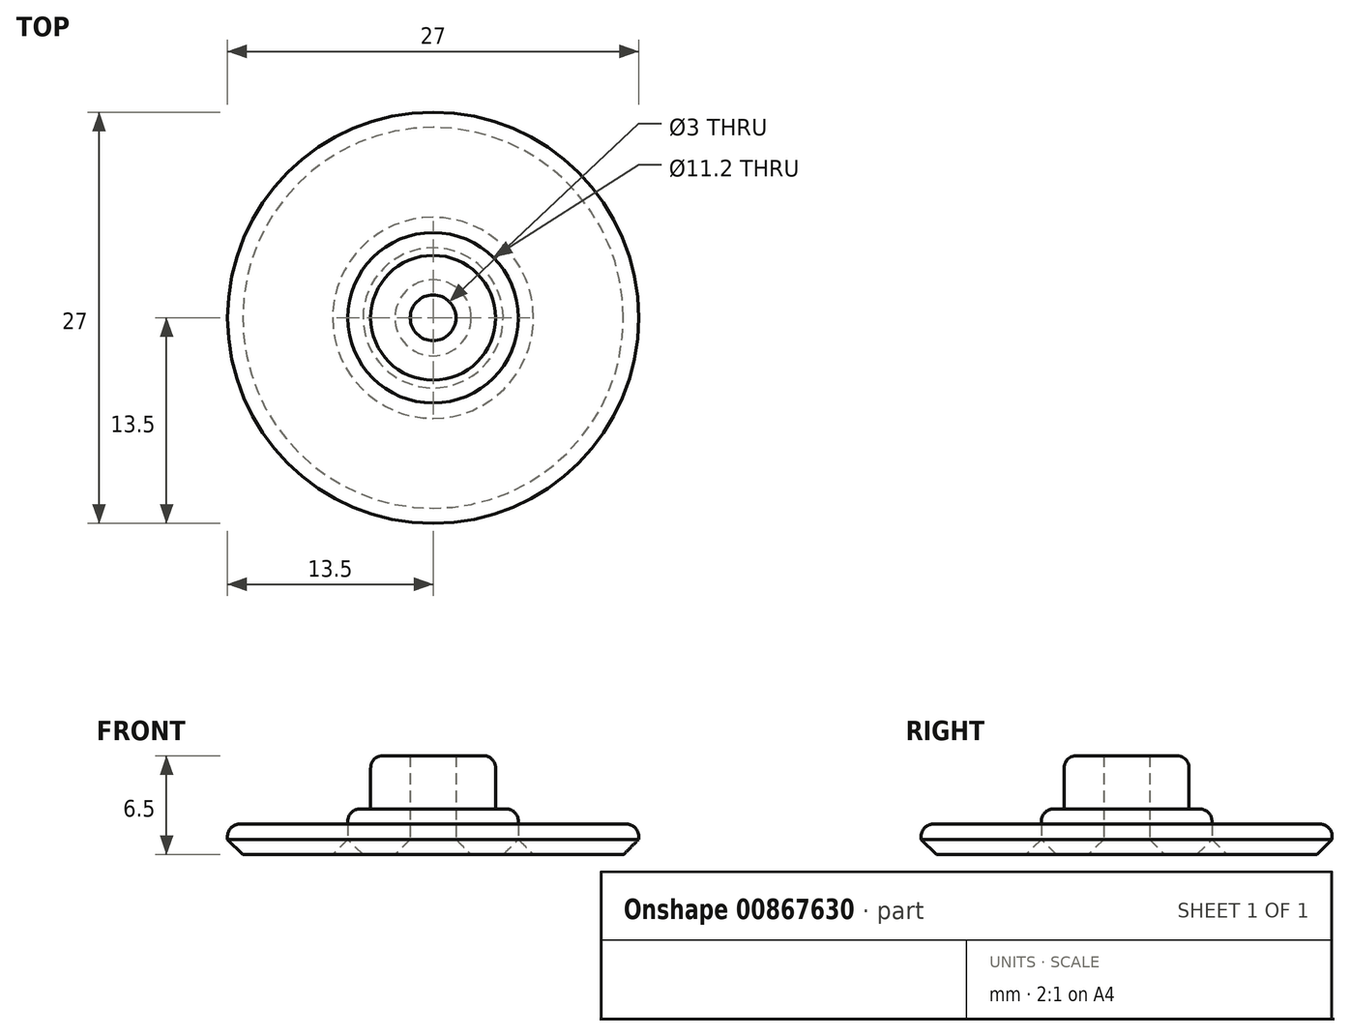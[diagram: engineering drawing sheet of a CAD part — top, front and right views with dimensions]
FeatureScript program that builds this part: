
annotation { "Feature Type Name" : "Feature", "Feature Type Description" : "" }
export const myFeature = defineFeature(function(context is Context, id is Id, definition is map)
    precondition{}
    {
        {
            var Q0;
            Q0=qCreatedBy(makeId("Top.planeOp"),FACE);
            var sketch = newSketch(context, id + "F0", { "sketchPlane" : qUnion([Q0])});
            skCircle(sketch, "E0", {"center": v(0, 0) * mm, "radius": 13.5 * mm});
            skCircle(sketch, "E1", {"center": v(0, 0) * mm, "radius": 5.6 * mm});
            skCircle(sketch, "E2", {"center": v(0, 0) * mm, "radius": 4.1 * mm});
            skCircle(sketch, "E3", {"center": v(0, 0) * mm, "radius": 1.5 * mm});
            skSolve(sketch);
        }
        {
            var Q0;
            Q0=makeQuery(id+"F0.imprint","IMPRINT",FACE,{"disambiguationData":[TD([[makeQuery(id+"F0.imprint","IMPRINT",EDGE,{"derivedFrom":sQuery(id+"F0.wireOp",EDGE,"E0")}),1.0]])]});
            extrude(context, id + "F1", {"entities" : qUnion([Q0]), "depth" : 2 * mm, "offsetDistance" : 25 * mm});
        }
        {
            var Q0;
            Q0=makeQuery(id+"F0.imprint","IMPRINT",FACE,{"disambiguationData":[TD([[makeQuery(id+"F0.imprint","IMPRINT",EDGE,{"derivedFrom":sQuery(id+"F0.wireOp",EDGE,"E1")}),1.0]])]});
            extrude(context, id + "F2", {"entities" : qUnion([Q0]), "depth" : 3 * mm, "offsetDistance" : 25 * mm});
        }
        {
            var Q0;
            Q0=makeQuery(id+"F0.imprint","IMPRINT",FACE,{"disambiguationData":[TD([[makeQuery(id+"F0.imprint","IMPRINT",EDGE,{"derivedFrom":sQuery(id+"F0.wireOp",EDGE,"E2")}),1.0]])]});
            extrude(context, id + "F3", {"entities" : qUnion([Q0]), "operationType" : NewBodyOperationType.ADD, "depth" : 6.5 * mm, "offsetDistance" : 25 * mm});
        }
        {
            var Q0;
            Q0=makeQuery(id+"F1.opExtrude","CAP_EDGE",EDGE,{"disambiguationData":[OSD([sQuery(id+"F0.wireOp",EDGE,"E0")])],"isStart":true});
            var Q1;
            Q1=makeQuery(id+"F1.opExtrude","CAP_EDGE",EDGE,{"disambiguationData":[OSD([sQuery(id+"F0.wireOp",EDGE,"E1")])],"isStart":true});
            var Q2;
            {var subQ0=sQuery(id+"F0.wireOp",EDGE,"E2");Q2=makeQuery(id+"F3.boolean.opBoolean","MERGE",FACE,{"derivedFrom":[makeQuery(id+"F2.opExtrude","CAP_FACE",FACE,{"disambiguationData":[OSD([sQuery(id+"F0.wireOp",EDGE,"E1"),subQ0])],"isStart":true}),makeQuery(id+"F3.opExtrude","CAP_FACE",FACE,{"disambiguationData":[OSD([subQ0])],"isStart":true})]});}
            chamfer(context, id + "F4", {"entities" : qUnion([Q0, Q1, Q2]), "width" : 1 * mm, "tangentPropagation" : true});
        }
        {
            var Q0;
            Q0=makeQuery(id+"F3.opExtrude","CAP_EDGE",EDGE,{"disambiguationData":[OSD([sQuery(id+"F0.wireOp",EDGE,"E2")])],"isStart":false});
            var Q1;
            Q1=makeQuery(id+"F1.opExtrude","CAP_EDGE",EDGE,{"disambiguationData":[OSD([sQuery(id+"F0.wireOp",EDGE,"E0")])],"isStart":false});
            var Q2;
            Q2=makeQuery(id+"F2.opExtrude","CAP_EDGE",EDGE,{"disambiguationData":[OSD([sQuery(id+"F0.wireOp",EDGE,"E1")])],"isStart":false});
            fillet(context, id + "F5", {"entities" : qUnion([Q0, Q1, Q2]), "radius" : .8 * mm, "tangentPropagation" : true, "allowEdgeOverflow" : false});
        }
    });
